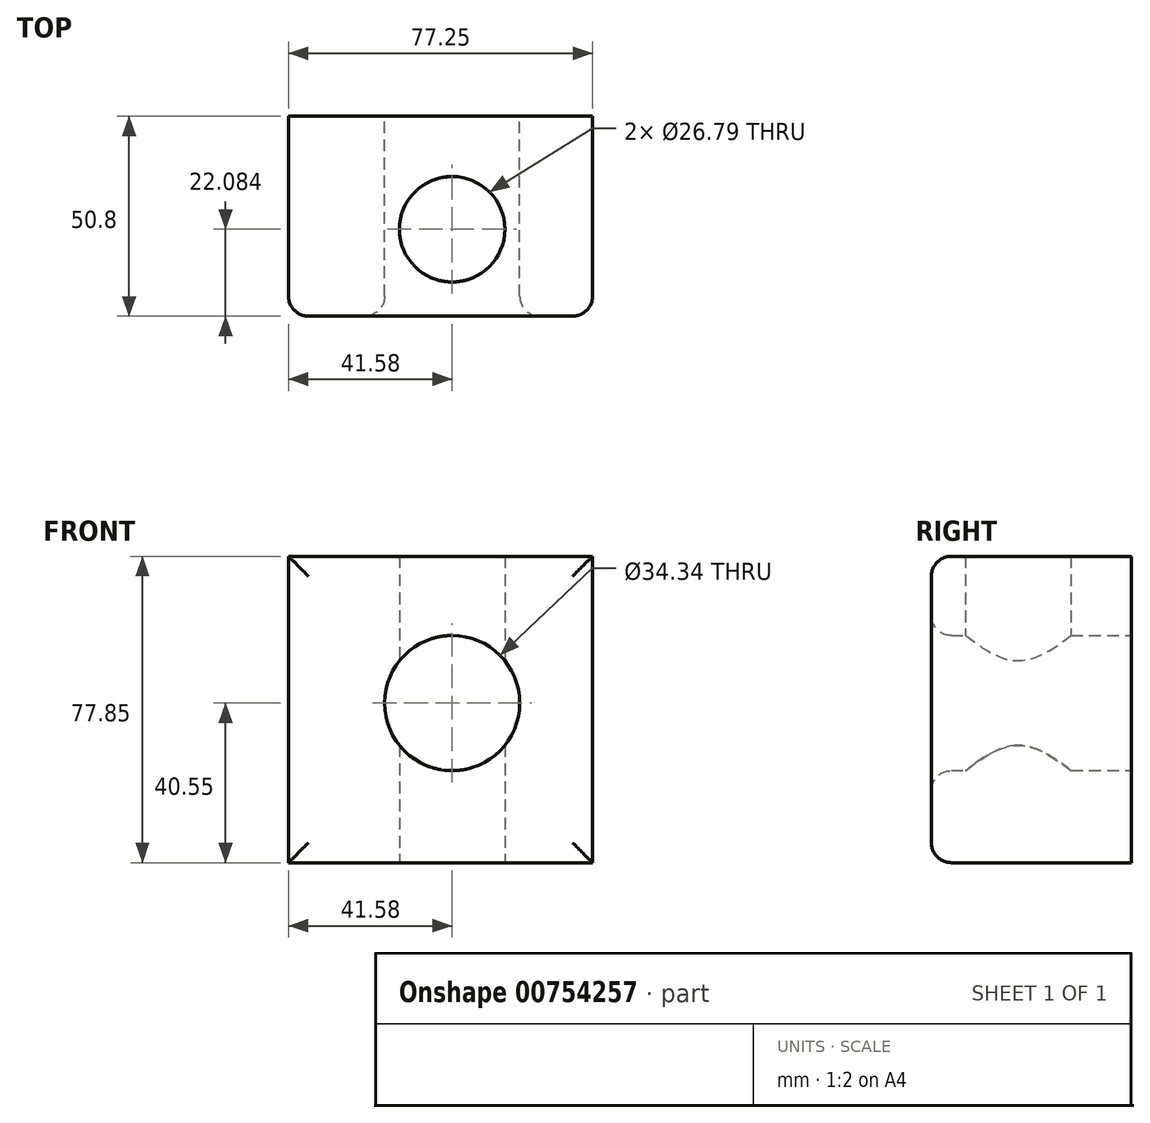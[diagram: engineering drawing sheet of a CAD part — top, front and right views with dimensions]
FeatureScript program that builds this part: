
annotation { "Feature Type Name" : "Feature", "Feature Type Description" : "" }
export const myFeature = defineFeature(function(context is Context, id is Id, definition is map)
    precondition{}
    {
        {
            var Q0;
            Q0=qCreatedBy(makeId("Front.planeOp"),FACE);
            var sketch = newSketch(context, id + "F0", { "sketchPlane" : qUnion([Q0])});
            skLineSegment(sketch, "E0.bottom", {"start": v(-41.58, -40.55) * mm, "end": v(35.67, -40.55) * mm});
            skLineSegment(sketch, "E0.top", {"start": v(-41.58, 37.3) * mm, "end": v(35.67, 37.3) * mm});
            skLineSegment(sketch, "E0.left", {"start": v(-41.58, -40.55) * mm, "end": v(-41.58, 37.3) * mm});
            skLineSegment(sketch, "E0.right", {"start": v(35.67, -40.55) * mm, "end": v(35.67, 37.3) * mm});
            skCircle(sketch, "E1", {"center": v(0, 0) * mm, "radius": 17.17 * mm});
            skSolve(sketch);
        }
        {
            var Q0;
            Q0 = qSketchRegion(id + "F0", true);
            extrude(context, id + "F1", {"entities" : qUnion([Q0]), "depth" : 50.8 * mm, "offsetDistance" : 25.4 * mm});
        }
        {
            var Q0;
            Q0=makeQuery(id+"F1.opExtrude","CAP_EDGE",EDGE,{"disambiguationData":[OSD([sQuery(id+"F0.wireOp",EDGE,"E0.bottom")])],"isStart":false});
            var Q1;
            Q1=makeQuery(id+"F1.opExtrude","CAP_EDGE",EDGE,{"disambiguationData":[OSD([sQuery(id+"F0.wireOp",EDGE,"E0.right")])],"isStart":false});
            var Q2;
            Q2=makeQuery(id+"F1.opExtrude","CAP_EDGE",EDGE,{"disambiguationData":[OSD([sQuery(id+"F0.wireOp",EDGE,"E0.top")])],"isStart":false});
            var Q3;
            Q3=makeQuery(id+"F1.opExtrude","CAP_EDGE",EDGE,{"disambiguationData":[OSD([sQuery(id+"F0.wireOp",EDGE,"E0.left")])],"isStart":false});
            var Q4;
            Q4=makeQuery(id+"F1.opExtrude","CAP_EDGE",EDGE,{"disambiguationData":[OSD([sQuery(id+"F0.wireOp",EDGE,"E1")])],"isStart":false});
            fillet(context, id + "F2", {"entities" : qUnion([Q0, Q1, Q2, Q3, Q4]), "radius" : 5.08 * mm, "tangentPropagation" : true, "allowEdgeOverflow" : false});
        }
        {
            var Q0;
            Q0=makeQuery(id+"F1.opExtrude","SWEPT_FACE",FACE,{"disambiguationData":[OSD([sQuery(id+"F0.wireOp",EDGE,"E0.bottom")])]});
            var sketch = newSketch(context, id + "F3", { "sketchPlane" : qUnion([Q0])});
            skCircle(sketch, "E2", {"center": v(0, 28.72) * mm, "radius": 13.4 * mm});
            skSolve(sketch);
        }
        {
            var Q0;
            Q0 = qSketchRegion(id + "F3", true);
            extrude(context, id + "F4", {"entities" : qUnion([Q0]), "operationType" : NewBodyOperationType.REMOVE, "oppositeDirection" : true, "depth" : 228.6 * mm, "offsetDistance" : 25.4 * mm});
        }
    });
